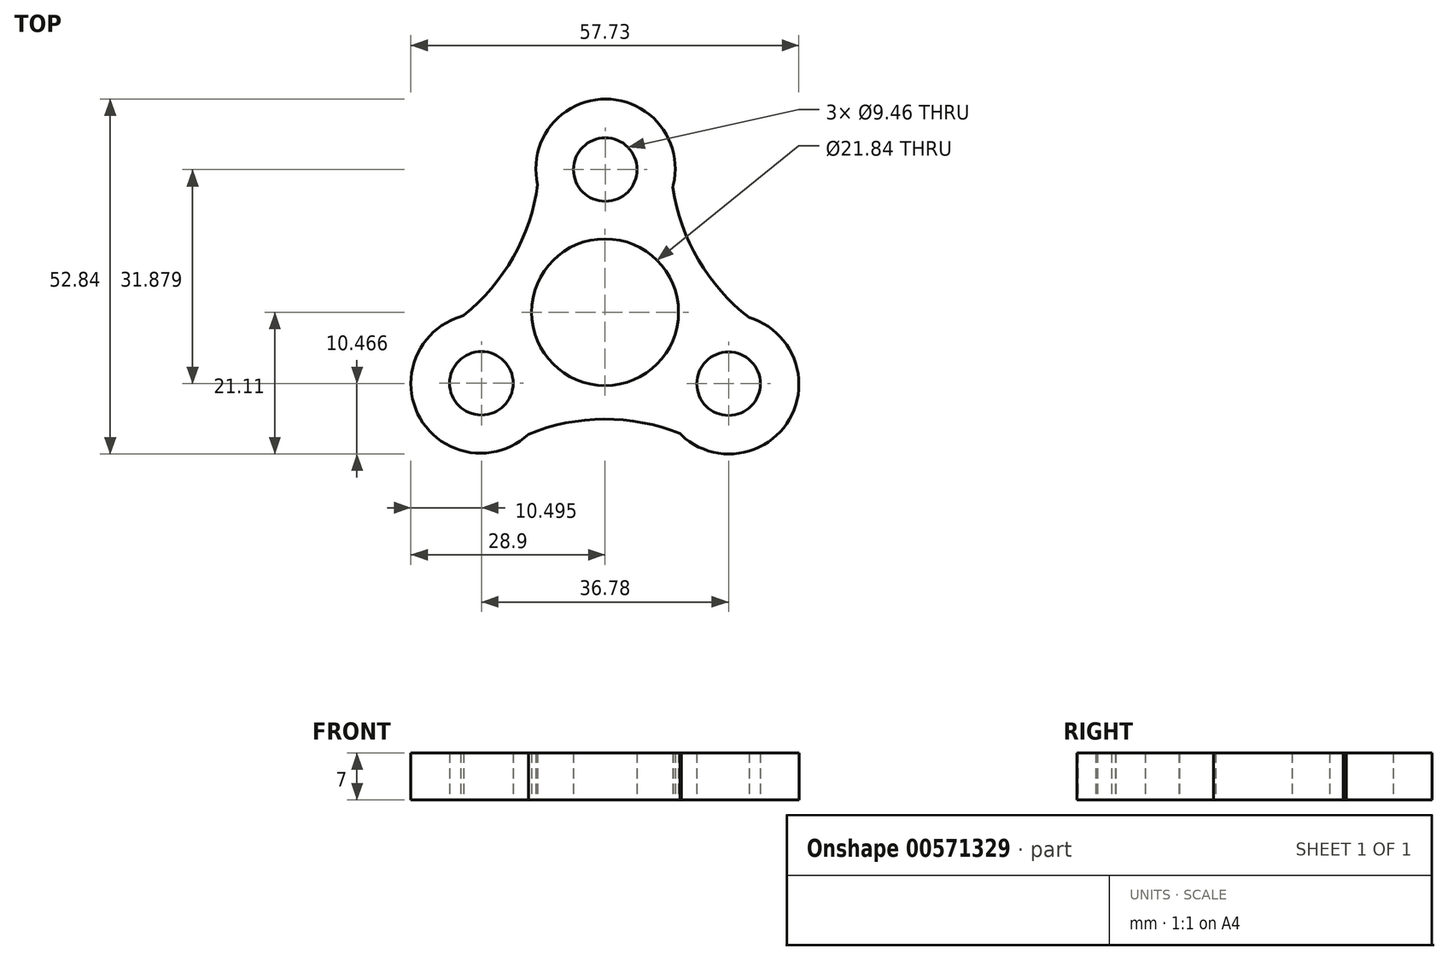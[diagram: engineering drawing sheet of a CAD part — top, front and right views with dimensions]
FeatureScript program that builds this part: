
annotation { "Feature Type Name" : "Feature", "Feature Type Description" : "" }
export const myFeature = defineFeature(function(context is Context, id is Id, definition is map)
    precondition{}
    {
        {
            var Q0;
            Q0=qCreatedBy(makeId("Top.planeOp"),FACE);
            var sketch = newSketch(context, id + "F0", { "sketchPlane" : qUnion([Q0])});
            skCircle(sketch, "E0", {"center": v(0, 0) * mm, "radius": 10.92 * mm});
            skArc(sketch, "E1", {"start": v(11.33, -18.27) * mm, "mid": v(27.44, -15.93) * mm, "end": v(21.45, -0.8) * mm});
            skArc(sketch, "E2.1.0", {"start": v(-0.03, 10.86) * mm, "mid": v(0.02, 10.86) * mm, "end": v(0.06, 10.86) * mm});
            skPoint(sketch, "E2.center", {"position": v(0.02, -0.07) * mm});
            skLineSegment(sketch, "E3.1.0", {"start": v(10.05, 18.95) * mm, "end": v(10.05, 18.95) * mm});
            skLineSegment(sketch, "E3.2.0", {"start": v(-21.47, -0.73) * mm, "end": v(-21.47, -0.73) * mm});
            skArc(sketch, "E4.trimOffspring", {"start": v(-9.33, -5.8) * mm, "mid": v(-9.5, -5.48) * mm, "end": v(-9.69, -5.17) * mm});
            skArc(sketch, "E5.1.0", {"start": v(-21.04, -0.46) * mm, "mid": v(-13.66, 8.2) * mm, "end": v(-10.03, 18.98) * mm});
            skArc(sketch, "E5.1.1", {"start": v(10.16, 18.95) * mm, "mid": v(0.08, 31.73) * mm, "end": v(-10.03, 18.98) * mm});
            skArc(sketch, "E5.2.0", {"start": v(11.15, -18.08) * mm, "mid": v(-0.14, -15.93) * mm, "end": v(-11.42, -18.17) * mm});
            skArc(sketch, "E5.2.1", {"start": v(-21.5, -0.68) * mm, "mid": v(-27.52, -15.8) * mm, "end": v(-11.42, -18.17) * mm});
            skCircle(sketch, "E6", {"center": v(0.03, 21.23) * mm, "radius": 4.73 * mm});
            skCircle(sketch, "E7.1.0", {"center": v(-18.4, -10.6) * mm, "radius": 4.73 * mm});
            skCircle(sketch, "E7.2.0", {"center": v(18.37, -10.64) * mm, "radius": 4.73 * mm});
            skLineSegment(sketch, "E8", {"start": v(10.16, 18.95) * mm, "end": v(10.1, 18.56) * mm});
            skArc(sketch, "E9.trimOffspring", {"start": v(10.1, 18.56) * mm, "mid": v(13.9, 7.78) * mm, "end": v(21.45, -0.8) * mm});
            skLineSegment(sketch, "E10", {"start": v(11.33, -18.27) * mm, "end": v(11.15, -18.08) * mm});
            skPoint(sketch, "E11.orphan", {"position": v(11.39, -18.17) * mm});
            skLineSegment(sketch, "E12", {"start": v(-21.5, -0.68) * mm, "end": v(-21.04, -0.46) * mm});
            skPoint(sketch, "E13.orphan", {"position": v(-21.43, -0.78) * mm});
            skSolve(sketch);
        }
        {
            var Q0;
            Q0=qSketchRegion(id+"F0",true);
            extrude(context, id + "F1", {"entities" : qUnion([Q0]), "depth" : 7 * mm, "offsetDistance" : 25 * mm});
        }
    });
